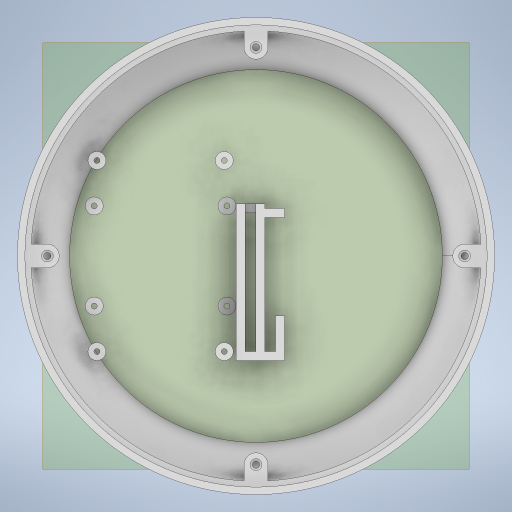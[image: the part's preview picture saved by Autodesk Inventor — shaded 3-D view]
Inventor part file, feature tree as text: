
AUTODESK INVENTOR PART (.ipt)
format: ipt  version: 2023.1 (Build 271208000, 208)  size: 599,552 bytes
history: native  units: mm
features: extrude x9, sketch x9, other x3, revolve x1, shell x1, chamfer x1, hole x1, pattern_circular x1
ambient origin geometry x8: Origin, YZ Plane, XZ Plane, XY Plane, X Axis, Y Axis, Z Axis, Center Point
bodies: Body1 (feature_tree)
feature tree (26):
  other  "솔리드1"
  revolve  "회전1"
  shell  "쉘1"  Thickness=120.0mm
  extrude  "돌출10"  Depth=140.0mm
  extrude  "돌출11"  Depth=60.0mm
  chamfer  "모따기1"  Distance=130.0mm
  hole  "구멍5"  [1 undecoded]
  pattern_circular  "원형 패턴1"  Angle=360.0deg  [1 undecoded]
  sketch  "스케치24"
  extrude  "돌출12"  Depth=4.0mm
  extrude  "돌출13"  Depth=5.0mm TaperAngle=0.0deg
  other  "작업 평면3"
  extrude  "돌출14"  Depth=155.0mm
  other  "작업 평면4"
  sketch  "스케치26"
  extrude  "돌출15"  Depth=8.0mm
  extrude  "돌출16"  Depth=70.0mm
  extrude  "돌출17"  Depth=10.0mm TaperAngle=0.0deg
  extrude  "돌출18"  Depth=2.0mm TaperAngle=45.0deg
  sketch  "스케치1"
  sketch  "스케치21"
  sketch  "스케치22"
  sketch  "스케치23"
  sketch  "스케치25"
  sketch  "스케치27"
  sketch  "스케치28"
note: 2 required parameter values undecoded (feature->parameter linkage not recoverable at this tier; creation-order binding heuristic only, values carry confidence <= 0.55)
